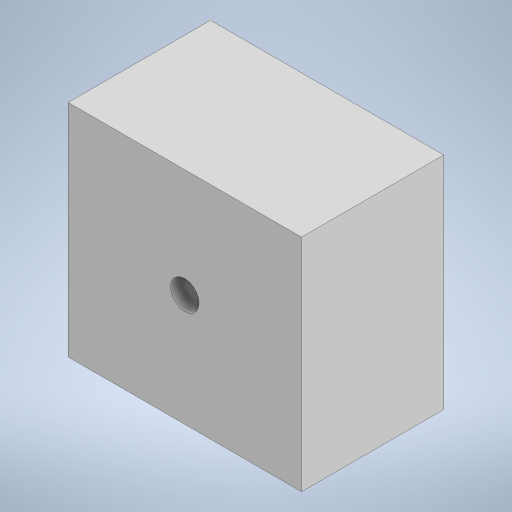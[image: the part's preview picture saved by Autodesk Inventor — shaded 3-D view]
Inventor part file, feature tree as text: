
AUTODESK INVENTOR PART (.ipt)
format: ipt  version: 2023.5 (Build 275446000, 446)  size: 173,056 bytes
history: native  units: in
note: dims shown in document units (in); Inventor stores cm internally (conversion verified against a paired STEP export)
features: sketch x3, extrude x2
ambient origin geometry x8: Origin, YZ Plane, XZ Plane, XY Plane, X Axis, Y Axis, Z Axis, Center Point
bodies: Solid1 (feature_tree)
feature tree (5):
  sketch  "Sketch1"  dims[d0=0.6457in d1=0.6102in]
  extrude  "Extrusion1"  Depth=0.6102in
  extrude  "Extrusion2"  Depth=0.3937in
  sketch  "Sketch2"  dims[d2=0.3937in d3=0.0in d4=0.0787in]
  sketch  "Sketch3"  dims[d5=0.0in d6=0.0in]
